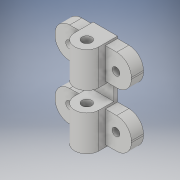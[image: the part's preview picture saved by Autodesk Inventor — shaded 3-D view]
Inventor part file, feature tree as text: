
AUTODESK INVENTOR PART (.ipt)
format: ipt  version: 2018 (Build 220112000, 112)  size: 199,168 bytes
history: native  units: in
note: dims shown in document units (in); Inventor stores cm internally (conversion verified against a paired STEP export)
features: extrude x6, sketch x4, fillet x2, plane x1
ambient origin geometry x8: Origin, YZ Plane, XZ Plane, XY Plane, X Axis, Y Axis, Z Axis, Center Point
bodies: Solid1 (feature_tree)
feature tree (13):
  sketch  "Sketch1"  dims[d0=0.3937in d1=1.46in]
  extrude  "Extrusion1"  Depth=1.46in
  extrude  "Extrusion2"  Depth=0.5in
  extrude  "Extrusion3"  Depth=0.5in
  fillet  "Fillet1"  Radius=0.4965in
  fillet  "Fillet2"  Radius=0.1969in
  extrude  "Extrusion4"  Depth=0.1969in
  extrude  "Extrusion5"  Depth=0.2362in
  plane  "Work Plane1"
  extrude  "Extrusion6"  Depth=0.315in
  sketch  "Sketch2"  dims[d2=0.42in d3=0.5in]
  sketch  "Sketch3"  dims[d4=0.42in d5=0.5in d6=0.4965in d7=0.0in d8=0.1969in d9=0.0in]
  sketch  "Sketch4"  dims[d10=0.1969in d11=0.0in d12=0.1969in d13=0.2362in d14=0.125in d15=0.85in d16=0.75in d17=0.125in d18=0.125in d19=0.125in d20=0.1969in d21=0.0in d22=0.1575in d23=3.937in d24=0.0in d25=0.4386in d26=0.315in d27=0.0in]
